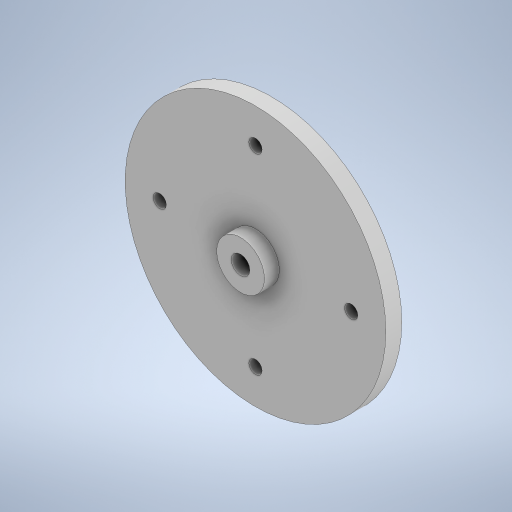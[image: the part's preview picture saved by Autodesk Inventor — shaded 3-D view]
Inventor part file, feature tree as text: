
AUTODESK INVENTOR PART (.ipt)
format: ipt  version: 2023.1 (Build 271208000, 208)  size: 250,368 bytes
history: native  units: mm
features: extrude x3, sketch x2, other x1
ambient origin geometry x8: Origin, YZ Plane, XZ Plane, XY Plane, X Axis, Y Axis, Z Axis, Center Point
bodies: Body1 (feature_tree)
feature tree (6):
  other  "솔리드1"
  sketch  "스케치1"
  extrude  "돌출1"  Depth=49.0mm
  extrude  "돌출2"  Depth=9.0mm
  extrude  "돌출3"  Depth=3.5mm
  sketch  "스케치2"
